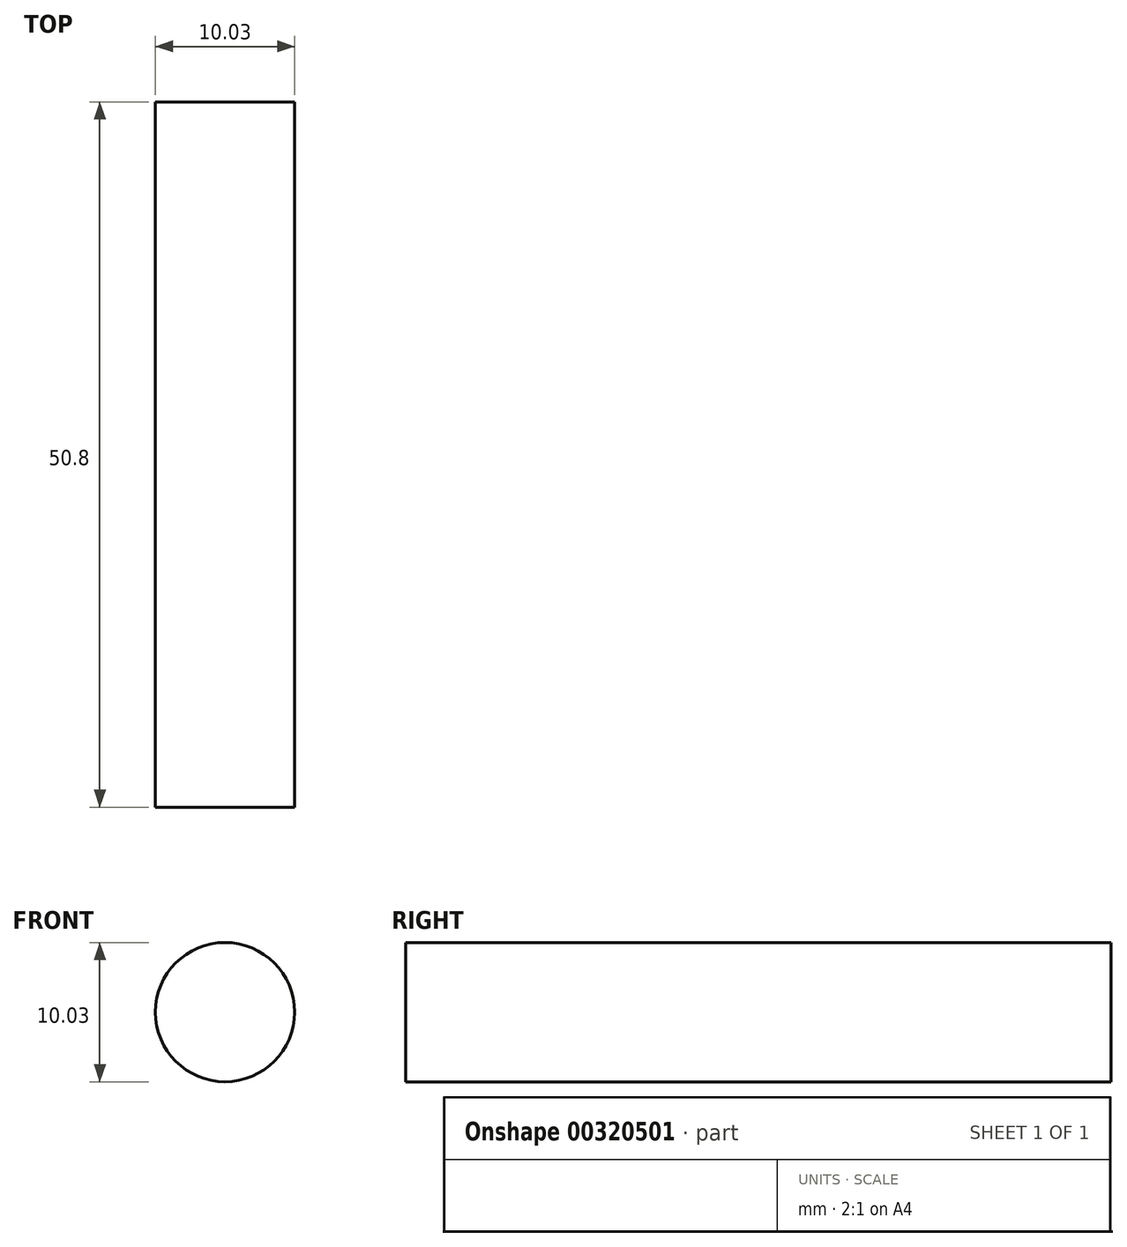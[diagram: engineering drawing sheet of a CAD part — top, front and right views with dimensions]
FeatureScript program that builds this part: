
annotation { "Feature Type Name" : "Feature", "Feature Type Description" : "" }
export const myFeature = defineFeature(function(context is Context, id is Id, definition is map)
    precondition{}
    {
        {
            var Q0;
            Q0=qCreatedBy(makeId("Front.planeOp"),FACE);
            var sketch = newSketch(context, id + "F0", { "sketchPlane" : qUnion([Q0])});
            skCircle(sketch, "E0", {"center": v(-9.08, 10.34) * mm, "radius": 5.02 * mm});
            skSolve(sketch);
        }
        {
            var Q0;
            Q0=makeQuery(id+"F0.imprint","IMPRINT",FACE,{"disambiguationData":[TD([[makeQuery(id+"F0.imprint","IMPRINT",EDGE,{"derivedFrom":sQuery(id+"F0.wireOp",EDGE,"E0")}),1.0]])]});
            extrude(context, id + "F1", {"entities" : qUnion([Q0]), "depth" : 50.8 * mm});
        }
    });
